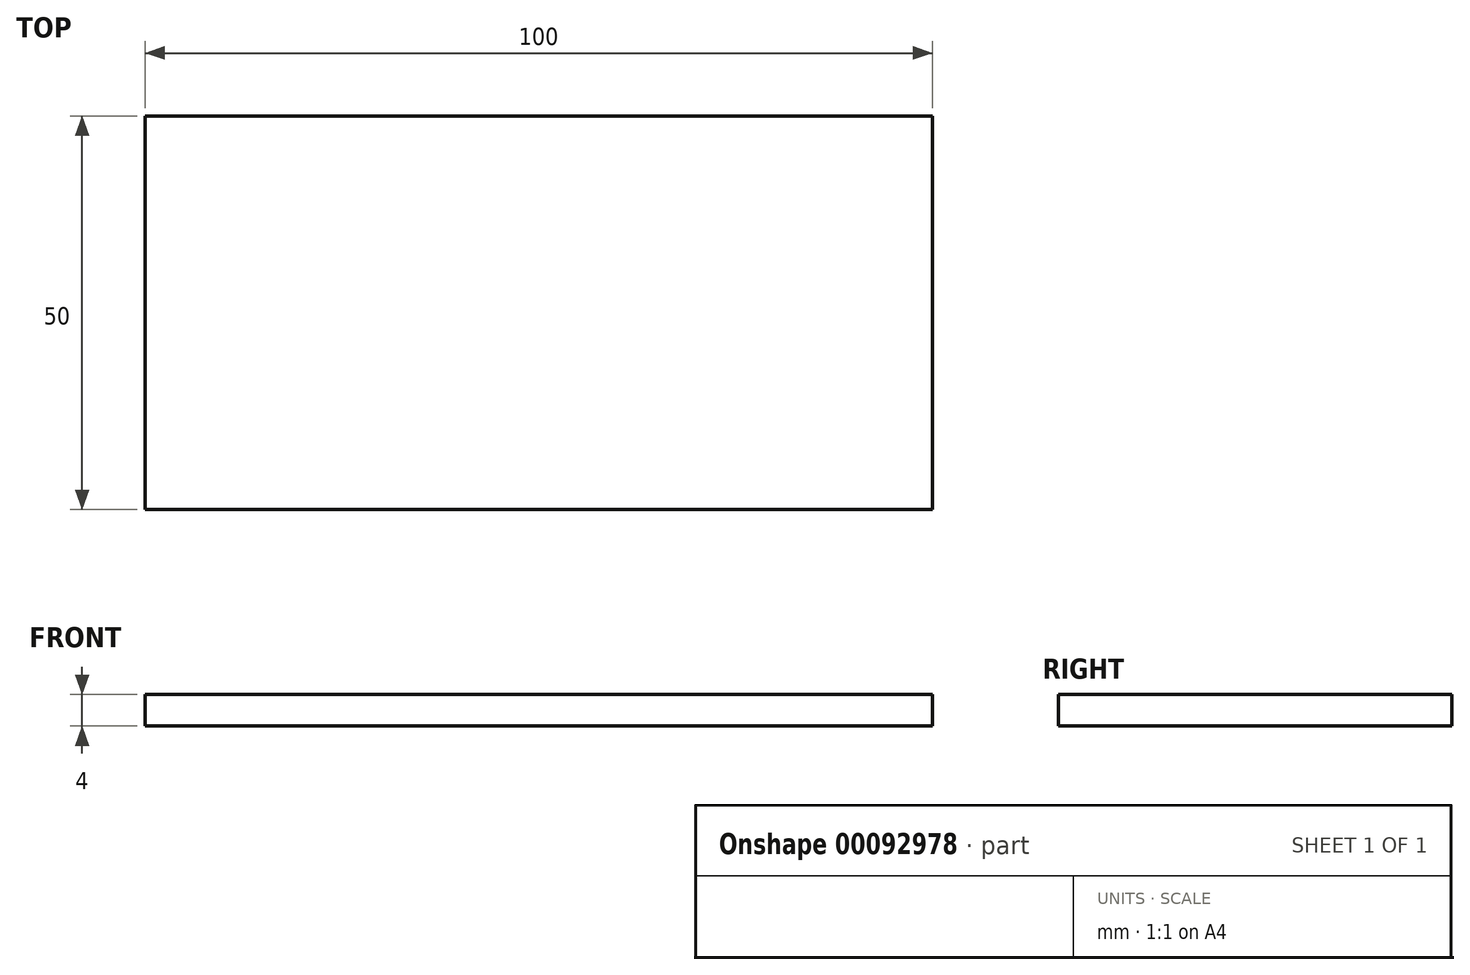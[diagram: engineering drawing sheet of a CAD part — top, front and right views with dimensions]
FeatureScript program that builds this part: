
annotation { "Feature Type Name" : "Feature", "Feature Type Description" : "" }
export const myFeature = defineFeature(function(context is Context, id is Id, definition is map)
    precondition{}
    {
        {
            var Q0;
            Q0=qCreatedBy(makeId("Top.planeOp"),FACE);
            var sketch = newSketch(context, id + "F0", { "sketchPlane" : qUnion([Q0])});
            skLineSegment(sketch, "E0.bottom", {"start": v(-50, 25) * mm, "end": v(50, 25) * mm});
            skLineSegment(sketch, "E0.top", {"start": v(-50, -25) * mm, "end": v(50, -25) * mm});
            skLineSegment(sketch, "E0.left", {"start": v(-50, 25) * mm, "end": v(-50, -25) * mm});
            skLineSegment(sketch, "E0.right", {"start": v(50, 25) * mm, "end": v(50, -25) * mm});
            skPoint(sketch, "E0.middle", {"position": v(0, 0) * mm});
            skSolve(sketch);
        }
        {
            var Q0;
            Q0 = qSketchRegion(id + "F0", true);
            var Q1;
            Q1=makeQuery(id+"F0.imprint","IMPRINT",FACE,{"disambiguationData":[TD([[makeQuery(id+"F0.imprint","IMPRINT",EDGE,{"derivedFrom":sQuery(id+"F0.wireOp",EDGE,"E0.bottom")}),-1.0]])]});
            extrude(context, id + "F1", {"entities" : qUnion([Q0, Q1]), "depth" : 4 * mm});
        }
    });
